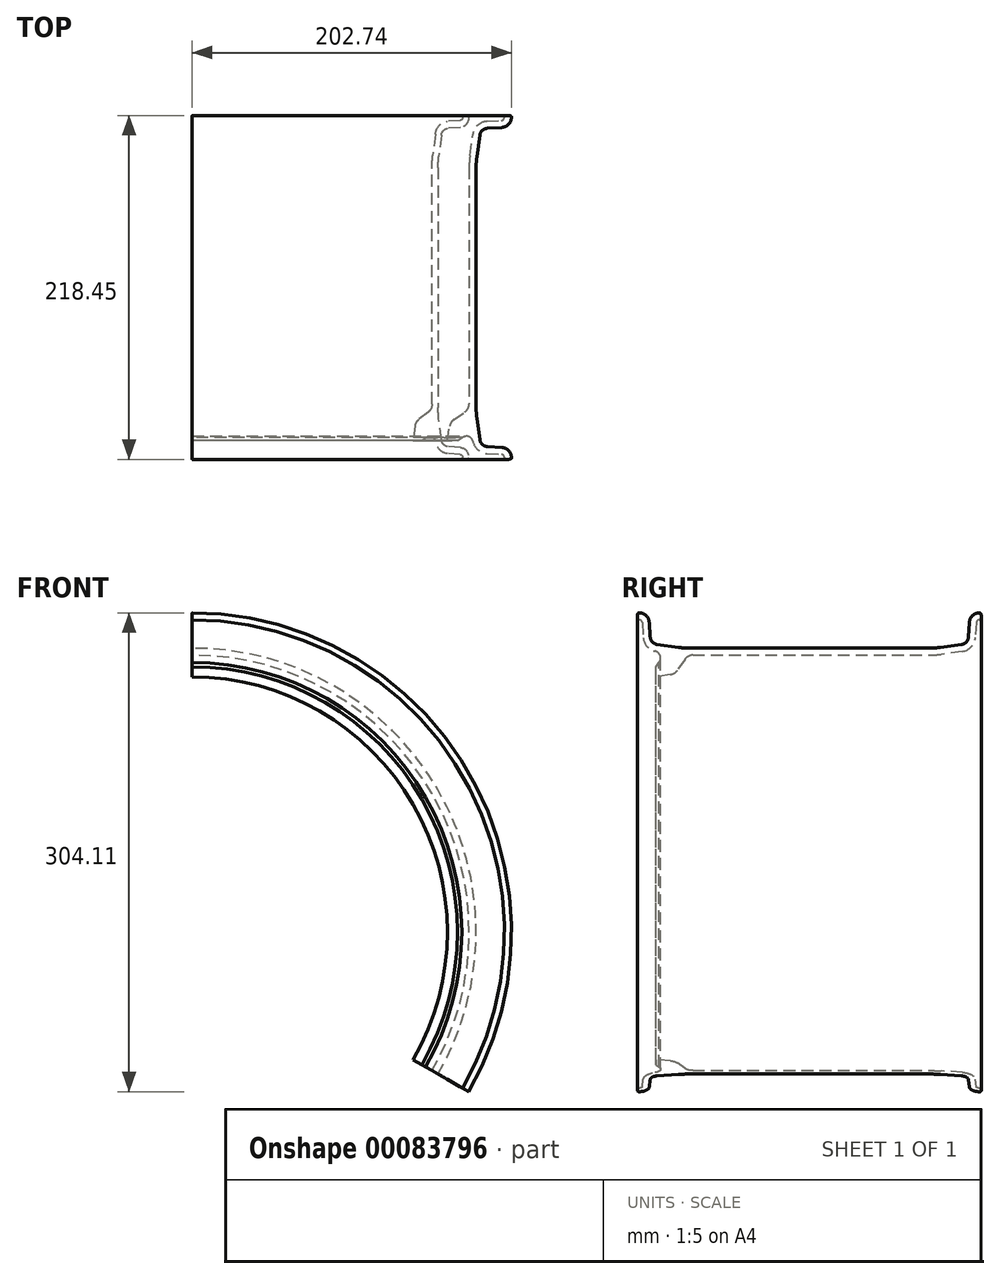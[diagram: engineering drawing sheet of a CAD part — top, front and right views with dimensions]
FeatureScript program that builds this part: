
annotation { "Feature Type Name" : "Feature", "Feature Type Description" : "" }
export const myFeature = defineFeature(function(context is Context, id is Id, definition is map)
    precondition{}
    {
        {
            var Q0;
            Q0=qCreatedBy(makeId("Right.planeOp"),FACE);
            var sketch = newSketch(context, id + "F0", { "sketchPlane" : qUnion([Q0])});
            skArc(sketch, "E0", {"start": v(7, 196.78) * mm, "mid": v(4.8, 201.2) * mm, "end": v(0.13, 202.72) * mm});
            skLineSegment(sketch, "E1", {"start": v(7, 196.78) * mm, "end": v(7.57, 187.43) * mm});
            skLineSegment(sketch, "E2", {"start": v(11.94, 182.71) * mm, "end": v(25.46, 180.84) * mm});
            skLineSegment(sketch, "E3", {"start": v(32.44, 180.36) * mm, "end": v(108.64, 180.36) * mm});
            skPoint(sketch, "E4.visualSharp", {"position": v(7.82, 183.29) * mm});
            skArc(sketch, "E4.filletArc", {"start": v(7.57, 187.43) * mm, "mid": v(8.91, 184.3) * mm, "end": v(11.94, 182.71) * mm});
            skPoint(sketch, "E5.visualSharp", {"position": v(28.93, 180.36) * mm});
            skArc(sketch, "E5.filletArc", {"start": v(25.46, 180.84) * mm, "mid": v(28.94, 180.48) * mm, "end": v(32.44, 180.36) * mm});
            skLineSegment(sketch, "E6.0", {"start": v(34.68, 175.91) * mm, "end": v(108.64, 175.91) * mm});
            skArc(sketch, "E6.2", {"start": v(2.56, 196.5) * mm, "mid": v(1.93, 197.8) * mm, "end": v(0.57, 198.3) * mm});
            skLineSegment(sketch, "E6.3", {"start": v(2.56, 196.5) * mm, "end": v(3.13, 187.16) * mm});
            skArc(sketch, "E6.4", {"start": v(3.13, 187.16) * mm, "mid": v(5.44, 181.5) * mm, "end": v(10.7, 178.42) * mm});
            skArc(sketch, "E7.MirrorCS", {"start": v(214.72, 196.5) * mm, "mid": v(215.39, 197.84) * mm, "end": v(216.82, 198.28) * mm});
            skArc(sketch, "E8.MirrorCS", {"start": v(191.82, 180.84) * mm, "mid": v(188.34, 180.48) * mm, "end": v(184.84, 180.36) * mm});
            skArc(sketch, "E9.MirrorCS", {"start": v(209.7, 187.43) * mm, "mid": v(208.36, 184.3) * mm, "end": v(205.34, 182.71) * mm});
            skArc(sketch, "E10.MirrorCS", {"start": v(214.14, 187.16) * mm, "mid": v(211.62, 181.27) * mm, "end": v(205.95, 178.31) * mm});
            skLineSegment(sketch, "E11.MirrorCS", {"start": v(214.72, 196.5) * mm, "end": v(214.14, 187.16) * mm});
            skArc(sketch, "E12.MirrorCS", {"start": v(210.28, 196.78) * mm, "mid": v(212.52, 201.23) * mm, "end": v(217.28, 202.7) * mm});
            skLineSegment(sketch, "E13.MirrorCS", {"start": v(205.95, 178.31) * mm, "end": v(192.43, 176.44) * mm});
            skPoint(sketch, "E14.MirrorP", {"position": v(188.34, 180.36) * mm});
            skPoint(sketch, "E15.MirrorP", {"position": v(209.45, 183.29) * mm});
            skArc(sketch, "E16.MirrorCS", {"start": v(192.43, 176.44) * mm, "mid": v(188.64, 176.04) * mm, "end": v(184.84, 175.91) * mm});
            skLineSegment(sketch, "E17.MirrorCS", {"start": v(205.34, 182.71) * mm, "end": v(191.82, 180.84) * mm});
            skLineSegment(sketch, "E18.MirrorCS", {"start": v(210.28, 196.78) * mm, "end": v(209.7, 187.43) * mm});
            skLineSegment(sketch, "E19.MirrorCS", {"start": v(184.84, 180.36) * mm, "end": v(108.64, 180.36) * mm});
            skLineSegment(sketch, "E20.MirrorCS", {"start": v(184.84, 175.91) * mm, "end": v(108.64, 175.91) * mm});
            skArc(sketch, "E21", {"start": v(-0.07, 202.6) * mm, "mid": v(-0.57, 200.4) * mm, "end": v(0.37, 198.37) * mm});
            skPoint(sketch, "E22.visualSharp", {"position": v(0, 202.7) * mm});
            skArc(sketch, "E22.filletArc", {"start": v(0.13, 202.72) * mm, "mid": v(0.01, 202.68) * mm, "end": v(-0.07, 202.6) * mm});
            skPoint(sketch, "E23.visualSharp", {"position": v(0.46, 198.28) * mm});
            skArc(sketch, "E23.filletArc", {"start": v(0.37, 198.37) * mm, "mid": v(0.46, 198.3) * mm, "end": v(0.57, 198.3) * mm});
            skArc(sketch, "E24.MirrorCS", {"start": v(217.15, 202.72) * mm, "mid": v(217.26, 202.68) * mm, "end": v(217.35, 202.6) * mm});
            skArc(sketch, "E25.MirrorCS", {"start": v(217.35, 202.6) * mm, "mid": v(217.84, 200.4) * mm, "end": v(216.9, 198.37) * mm});
            skArc(sketch, "E26.MirrorCS", {"start": v(216.9, 198.37) * mm, "mid": v(216.81, 198.3) * mm, "end": v(216.7, 198.3) * mm});
            skArc(sketch, "E27.MirrorCS", {"start": v(214.72, 196.5) * mm, "mid": v(215.35, 197.8) * mm, "end": v(216.7, 198.3) * mm});
            skPoint(sketch, "E28.MirrorP", {"position": v(216.82, 198.28) * mm});
            skPoint(sketch, "E29.MirrorP", {"position": v(217.28, 202.7) * mm});
            skArc(sketch, "E30.MirrorCS", {"start": v(210.28, 196.78) * mm, "mid": v(212.47, 201.2) * mm, "end": v(217.15, 202.72) * mm});
            skLineSegment(sketch, "E31", {"start": v(29.52, 173.2) * mm, "end": v(24.74, 166.22) * mm});
            skLineSegment(sketch, "E32", {"start": v(20.58, 163.58) * mm, "end": v(11.36, 162.1) * mm});
            skLineSegment(sketch, "E33", {"start": v(11.36, 162.1) * mm, "end": v(11.36, 168.5) * mm});
            skLineSegment(sketch, "E34", {"start": v(11.36, 168.5) * mm, "end": v(13.24, 171.24) * mm});
            skArc(sketch, "E35", {"start": v(13.24, 171.24) * mm, "mid": v(14.16, 173.88) * mm, "end": v(13.4, 176.57) * mm});
            skPoint(sketch, "E36.visualSharp", {"position": v(11.36, 178.3) * mm});
            skArc(sketch, "E36.filletArc", {"start": v(13.4, 176.57) * mm, "mid": v(12.24, 177.77) * mm, "end": v(10.7, 178.42) * mm});
            skPoint(sketch, "E37.visualSharp", {"position": v(31.38, 175.91) * mm});
            skArc(sketch, "E37.filletArc", {"start": v(34.68, 175.91) * mm, "mid": v(31.76, 175.2) * mm, "end": v(29.52, 173.2) * mm});
            skPoint(sketch, "E38.visualSharp", {"position": v(23.23, 164) * mm});
            skArc(sketch, "E38.filletArc", {"start": v(20.58, 163.58) * mm, "mid": v(22.93, 164.47) * mm, "end": v(24.74, 166.22) * mm});
            skLineSegment(sketch, "E39", {"start": v(0, 0) * mm, "end": v(195.67, 0) * mm});
            skSolve(sketch);
        }
        {
            var Q0;
            Q0=makeQuery(id+"F0.imprint","IMPRINT",FACE,{"disambiguationData":[TD([[makeQuery(id+"F0.imprint","IMPRINT",EDGE,{"derivedFrom":sQuery(id+"F0.wireOp",EDGE,"E0")}),1.0]])]});
            var Q1;
            Q1=sQuery(id+"F0.wireOp",EDGE,"E39");
            revolve(context, id + "F1", {"entities" : qUnion([Q0]), "axis" : qUnion([Q1]), "revolveType" : RevolveType.ONE_DIRECTION, "angle" : 120 * degree});
        }
    });
